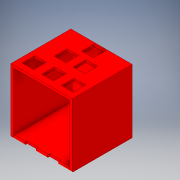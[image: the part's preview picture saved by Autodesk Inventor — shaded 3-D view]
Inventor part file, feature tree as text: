
AUTODESK INVENTOR PART (.ipt)
format: ipt  version: 2018 (Build 220112000, 112)  size: 254,976 bytes
history: native  units: in
note: dims shown in document units (in); Inventor stores cm internally (conversion verified against a paired STEP export)
features: sketch x11, extrude x10, shell x2, fillet x1
ambient origin geometry x8: Origin, YZ Plane, XZ Plane, XY Plane, X Axis, Y Axis, Z Axis, Center Point
bodies: Solid1 (feature_tree)
feature tree (24):
  extrude  "Extrusion1"  Depth=6.0in
  shell  "Shell1"  Thickness=6.0in
  extrude  "Extrusion6"  Depth=0.25in TaperAngle=0.0deg
  extrude  "Extrusion10"  Depth=1.1in
  extrude  "Extrusion11"  Depth=1.1in
  fillet  "Fillet1"  Radius=0.25in
  extrude  "Extrusion12"  Depth=0.125in
  shell  "Shell2"  Thickness=0.125in
  extrude  "Extrusion13"  Depth=0.125in
  sketch  "Sketch14"  dims[d69=6.0in d70=5.5in]
  extrude  "Extrusion18"  Depth=5.5in
  extrude  "Extrusion19"  Depth=0.25in
  extrude  "Extrusion22"  Depth=0.25in TaperAngle=0.0deg
  extrude  "Extrusion23"  Depth=1.25in
  sketch  "Sketch1"  dims[d0=6.0in d1=6.0in d2=6.0in d3=0.0in]
  sketch  "Sketch6"  dims[d4=0.25in d36=0.25in d37=0.0in]
  sketch  "Sketch10"  dims[d55=1.1in d56=1.1in]
  sketch  "Sketch11"  dims[d57=1.1in d58=1.1in d59=0.25in d60=0.0in]
  sketch  "Sketch12"  dims[d61=0.2in d62=0.125in d63=0.125in]
  sketch  "Sketch13"  dims[d64=1.8125in d65=5.0in d66=0.0in d67=0.0in d68=0.125in]
  sketch  "Sketch22"  dims[d71=3.5in d72=0.0in d73=0.25in]
  sketch  "Sketch23"  dims[d75=2.0in d76=0.0in d100=0.25in d101=0.0in]
  sketch  "Sketch27"  dims[d120=1.15in d121=1.25in]
  sketch  "Sketch28"  dims[d122=1.15in d123=1.25in d128=1.15in d129=1.25in d130=0.5in d131=0.5in d132=0.775in d133=0.6in d134=0.6in d135=0.6in d136=2.0in d142=1.5in d143=1.5in d144=1.15in d145=2.0in d147=1.15in d148=1.25in d149=2.425in d150=1.15in d151=1.25in d152=1.25in d153=0.25in d154=0.0in d169=0.1in d170=0.1in d171=0.11in d172=0.11in d173=0.3in d174=0.0in d176=1.0in d177=3.625in d178=0.0in]
